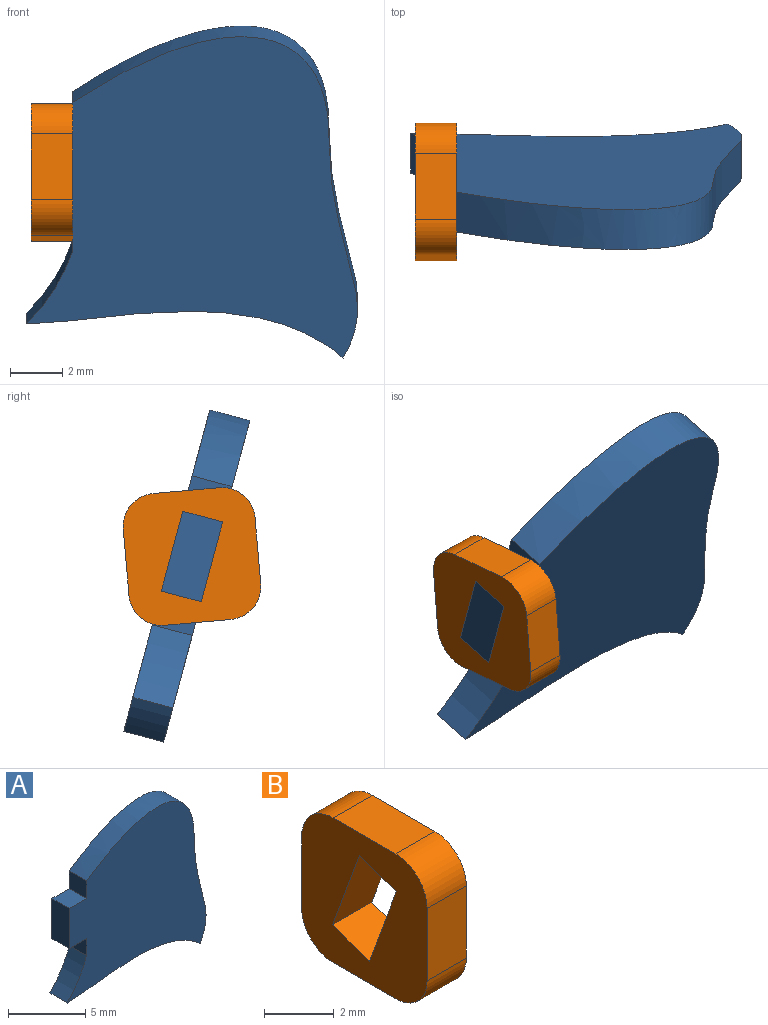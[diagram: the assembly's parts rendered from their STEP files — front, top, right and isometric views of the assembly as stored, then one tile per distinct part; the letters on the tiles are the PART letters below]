
ASSEMBLY  parts=2 mates=1
PART A: 11 faces, bbox 13x1.6x13.6 mm
  f0: plane 3.18x1.59mm, normal (-1,0,0), area 5mm2, adj f1,f6,f7,f8
  f1: plane 1.59x1.59mm, normal (0,0,-1), area 2.5mm2, adj f0,f2,f7,f8
  f2: plane 1.59x1.34mm, normal (-1,0,0), area 2.1mm2, adj f1,f3,f7,f8
  f3: extruded ~2.88x1.77mm, area 5.4mm2, adj f2,f4,f7,f8
  f4: extruded ~12.16x1.86mm, area 20mm2, adj f3,f5,f7,f8
  f5: extruded ~8.75x1.59mm, area 14.2mm2, adj f4,f7,f8,f10
  f6: plane 1.59x1.59mm, normal (0,0,1), area 2.5mm2, adj f0,f7,f8,f9
  f7: plane 13.56x13.03mm, normal (0,-1,0), area 113.6mm2, adj f0,f1,f2,f3,f4,f5,f6,f9
  f8: plane 13.56x13.03mm, normal (0,1,0), area 113.6mm2, adj f0,f1,f2,f3,f4,f5,f6,f9
  f9: plane 1.59x1.4mm, normal (-1,0,0), area 2.2mm2, adj f6,f7,f8,f10
  f10: extruded ~9.84x4.02mm, area 20.7mm2, adj f5,f7,f8,f9
PART B: 14 faces, bbox 1.6x5.1x5.1 mm
  f0: plane 2.98x1.59mm, normal (0,0.94,0.34), area 5mm2, adj f1,f7,f8,f9
  f1: plane 1.59x1.49mm, normal (0,0.34,-0.94), area 2.5mm2, adj f0,f2,f8,f9
  f2: plane 2.98x1.59mm, normal (0,-0.94,-0.34), area 5mm2, adj f1,f7,f8,f9
  f3: plane 2.54x1.59mm, normal (0,-1,0), area 4mm2, adj f8,f9,f10,f13
  f4: plane 2.54x1.59mm, normal (0,0,-1), area 4mm2, adj f8,f9,f10,f11
  f5: plane 2.54x1.59mm, normal (0,1,0), area 4mm2, adj f8,f9,f11,f12
  f6: plane 2.54x1.59mm, normal (0,0,1), area 4mm2, adj f8,f9,f12,f13
  f7: plane 1.59x1.49mm, normal (0,-0.34,0.94), area 2.5mm2, adj f0,f2,f8,f9
  f8: plane 5.08x5.08mm, normal (1,0,0), area 19.4mm2, adj f0,f1,f2,f3,f4,f5,f6,f7
  f9: plane 5.08x5.08mm, normal (-1,0,0), area 19.4mm2, adj f0,f1,f2,f3,f4,f5,f6,f7
  f10: cylinder r=1.27mm len=1.59mm, axis (1,0,0), area 3.2mm2, adj f3,f4,f8,f9
  f11: cylinder r=1.27mm len=1.59mm, axis (-1,0,0), area 3.2mm2, adj f4,f5,f8,f9
  f12: cylinder r=1.27mm len=1.59mm, axis (1,0,0), area 3.2mm2, adj f5,f6,f8,f9
  f13: cylinder r=1.27mm len=1.59mm, axis (-1,0,0), area 3.2mm2, adj f3,f6,f8,f9
PLACE A rot(axis=(1,0,0),15deg) t=(0,2.77,1.21)mm
PLACE B rot(axis=(-1,0,0),5deg) t=(0,-1.16,0.23)mm
MATE fastened A.f6 <-> B.f1  axis (0,-0.26,0.97) through (0,0.41,3.87)mm
